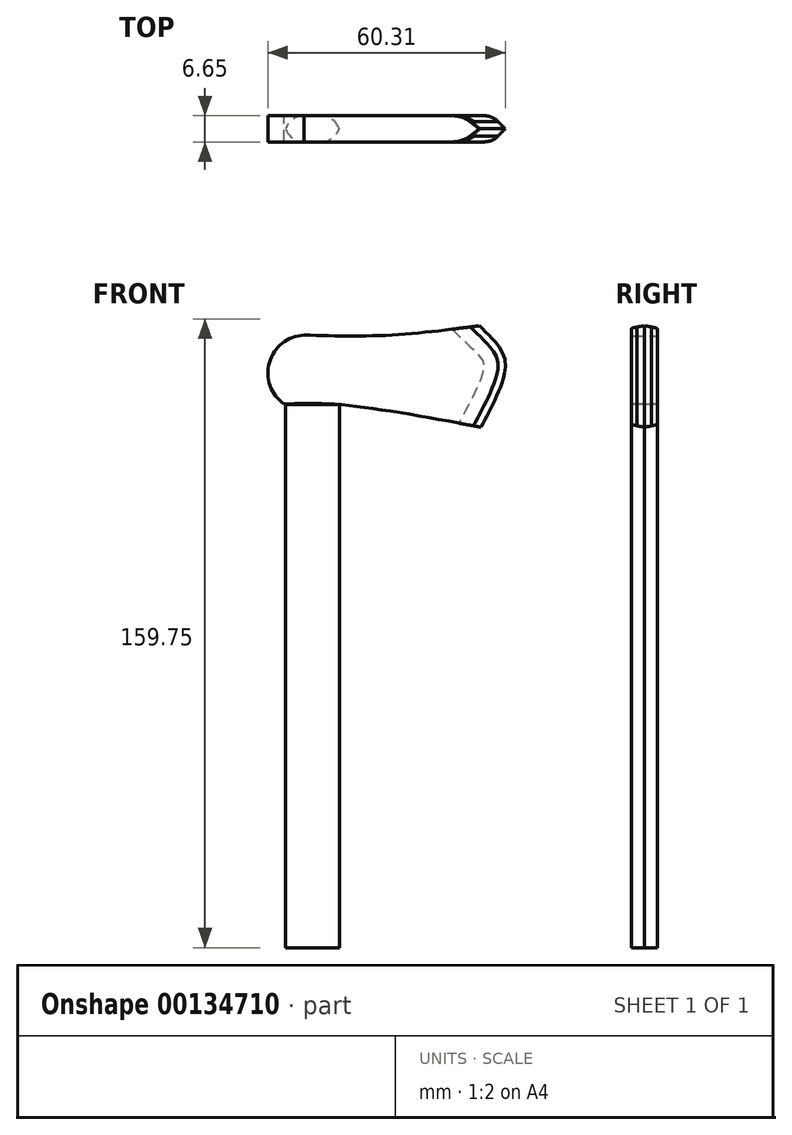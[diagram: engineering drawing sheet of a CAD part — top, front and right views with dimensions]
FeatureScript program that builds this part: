
annotation { "Feature Type Name" : "Feature", "Feature Type Description" : "" }
export const myFeature = defineFeature(function(context is Context, id is Id, definition is map)
    precondition{}
    {
        {
            var Q0;
            Q0=qCreatedBy(makeId("Front.planeOp"),FACE);
            var sketch = newSketch(context, id + "F0", { "sketchPlane" : qUnion([Q0])});
            skLineSegment(sketch, "E0", {"start": v(-26.57, 56.26) * mm, "end": v(-26.57, -81.79) * mm});
            skLineSegment(sketch, "E1", {"start": v(-26.57, -81.79) * mm, "end": v(-12.32, -81.79) * mm});
            skLineSegment(sketch, "E2", {"start": v(-12.32, -81.79) * mm, "end": v(-12.32, 56.26) * mm});
            skLineSegment(sketch, "E3", {"start": v(-12.32, 56.26) * mm, "end": v(-26.57, 56.26) * mm});
            skSolve(sketch);
        }
        {
            var Q0;
            Q0=qCreatedBy(makeId("Front.planeOp"),FACE);
            var sketch = newSketch(context, id + "F1", { "sketchPlane" : qUnion([Q0])});
            skArc(sketch, "E4", {"start": v(-21.61, 73.87) * mm, "mid": v(-30.38, 66.91) * mm, "end": v(-26.66, 56.36) * mm});
            skFitSpline(sketch, "E5", {"points": [v(-21.61, 73.87) * mm, v(0, 73.87) * mm, v(25.15, 76.54) * mm], "startDerivative": vector(44.17, -1.23) * mm, "endDerivative": vector(49.28, 6.48) * mm});
            skFitSpline(sketch, "E6", {"points": [v(25.15, 76.54) * mm, v(31.23, 67.49) * mm, v(25.15, 50.12) * mm], "startDerivative": vector(19.38, -18.66) * mm, "endDerivative": vector(-17.77, -33.54) * mm});
            skFitSpline(sketch, "E7", {"points": [v(25.15, 50.12) * mm, v(-12.4, 56.2) * mm, v(-26.66, 56.36) * mm], "startDerivative": vector(-67.68, 12.73) * mm, "endDerivative": vector(-33.17, -1.4) * mm});
            skSolve(sketch);
        }
        {
            var Q0;
            Q0 = qSketchRegion(id + "F0", true);
            var Q1;
            Q1 = qSketchRegion(id + "F1", true);
            extrude(context, id + "F2", {"entities" : qUnion([Q0, Q1]), "depth" : 6.65 * mm});
        }
        {
            var Q0;
            Q0=makeQuery(id+"F2.opExtrude","CAP_EDGE",EDGE,{"disambiguationData":[OSD([sQuery(id+"F0.wireOp",EDGE,"E0")])],"isStart":false});
            var Q1;
            Q1=makeQuery(id+"F2.opExtrude","CAP_EDGE",EDGE,{"disambiguationData":[OSD([sQuery(id+"F0.wireOp",EDGE,"E2")])],"isStart":false});
            var Q2;
            Q2=makeQuery(id+"F2.opExtrude","CAP_EDGE",EDGE,{"disambiguationData":[OSD([sQuery(id+"F0.wireOp",EDGE,"E0")])],"isStart":true});
            var Q3;
            Q3=makeQuery(id+"F2.opExtrude","CAP_EDGE",EDGE,{"disambiguationData":[OSD([sQuery(id+"F0.wireOp",EDGE,"E2")])],"isStart":true});
            fillet(context, id + "F3", {"entities" : qUnion([Q0, Q1, Q2, Q3]), "radius" : 5.08 * mm, "tangentPropagation" : true, "allowEdgeOverflow" : false});
        }
        {
            var Q0;
            Q0=makeQuery(id+"F2.opExtrude","CAP_EDGE",EDGE,{"disambiguationData":[OSD([sQuery(id+"F1.wireOp",EDGE,"E6")])],"isStart":false});
            var Q1;
            Q1=makeQuery(id+"F2.opExtrude","CAP_EDGE",EDGE,{"disambiguationData":[OSD([sQuery(id+"F1.wireOp",EDGE,"E6")])],"isStart":true});
            chamfer(context, id + "F4", {"entities" : qUnion([Q0, Q1]), "width" : 5.08 * mm, "tangentPropagation" : true});
        }
        {
            var Q0;
            {var subQ0=sQuery(id+"F1.wireOp",EDGE,"E6");Q0=makeQuery(id+"F4.opChamfer","BLEND_EDGE",EDGE,{"blendedFrom":[makeQuery(id+"F2.opExtrude","CAP_EDGE",EDGE,{"disambiguationData":[OSD([subQ0])],"isStart":true}),makeQuery(id+"F2.opExtrude","CAP_FACE",FACE,{"disambiguationData":[OSD([sQuery(id+"F1.wireOp",EDGE,"E4"),sQuery(id+"F1.wireOp",EDGE,"E5"),subQ0,sQuery(id+"F1.wireOp",EDGE,"E7")])],"isStart":true})],"blendedInto":[makeQuery(id+"F2.opExtrude","CAP_FACE",FACE,{"disambiguationData":[OSD([sQuery(id+"F1.wireOp",EDGE,"E4"),sQuery(id+"F1.wireOp",EDGE,"E5"),subQ0,sQuery(id+"F1.wireOp",EDGE,"E7")])],"isStart":true})]});}
            var Q1;
            {var subQ0=sQuery(id+"F1.wireOp",EDGE,"E6");Q1=makeQuery(id+"F4.opChamfer","BLEND_EDGE",EDGE,{"blendedFrom":[makeQuery(id+"F2.opExtrude","CAP_EDGE",EDGE,{"disambiguationData":[OSD([subQ0])],"isStart":false}),makeQuery(id+"F2.opExtrude","CAP_FACE",FACE,{"disambiguationData":[OSD([sQuery(id+"F1.wireOp",EDGE,"E4"),sQuery(id+"F1.wireOp",EDGE,"E5"),subQ0,sQuery(id+"F1.wireOp",EDGE,"E7")])],"isStart":false})],"blendedInto":[makeQuery(id+"F2.opExtrude","CAP_FACE",FACE,{"disambiguationData":[OSD([sQuery(id+"F1.wireOp",EDGE,"E4"),sQuery(id+"F1.wireOp",EDGE,"E5"),subQ0,sQuery(id+"F1.wireOp",EDGE,"E7")])],"isStart":false})]});}
            fillet(context, id + "F5", {"entities" : qUnion([Q0, Q1]), "radius" : 5.08 * mm, "tangentPropagation" : true, "allowEdgeOverflow" : false});
        }
    });
